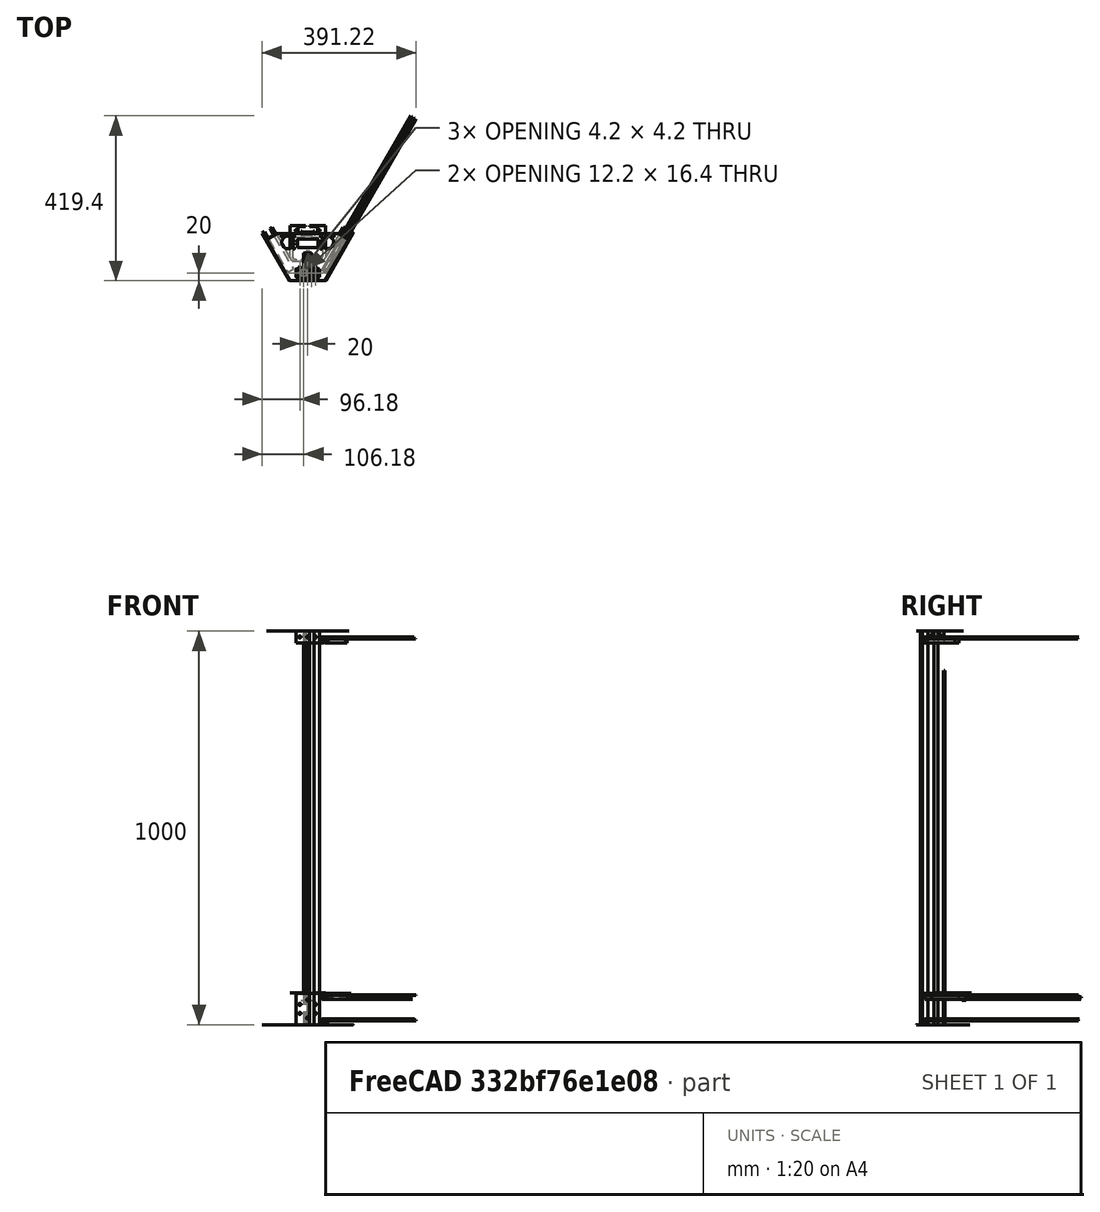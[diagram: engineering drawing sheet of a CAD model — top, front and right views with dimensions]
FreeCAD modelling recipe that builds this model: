
FCSTD DOCUMENT  (FreeCAD 2022.430R26244 +4758 (Git))
Label: SubAs3Column
License: All rights reserved
LicenseURL: http://en.wikipedia.org/wiki/All_rights_reserved
objects: App::FeaturePython×82, Part::FeaturePython×48, App::Link×8, App::LinkElement×3
note: 47 computed .brp shape members not serialized (recipe doc carries the construction recipe); baked Part::Feature solids carry a one-line shape summary decoded from their .brp
EXTERNAL_REF file=as3bottom_corner-M3x10.FCStd obj=Assembly
EXTERNAL_REF file=as3V-Slot 20x40x1000 Linear Rail.FCStd obj=Assembly
EXTERNAL_REF file=as3V-Slot 20x60x1000 Linear Rail.FCStd obj=Assembly
EXTERNAL_REF file=as3OpenBeam450mm.FCStd obj=Assembly
EXTERNAL_REF file=as3MotorFrame.FCStd obj=Assembly
EXTERNAL_REF file=As3NEMA 17.FCStd obj=Assembly
EXTERNAL_REF file=As3TopCorner.FCStd obj=Assembly
EXTERNAL_REF file=as3MGNR9R900CM-HiwinCorporation-3D-10-31-2021.FCStd obj=Assembly

FEATURE [App::Link] Link  label="As3bottom_corner-M3x10"
  AutoLinkLabel = false
  AutoPlacement = true
  LinkedObject = -> <external as3bottom_corner-M3x10.FCStd>#Assembly
  SyncGroupVisibility = false
  TreeRank = 0
  _LinkOwner = 170
  _LinkVersion = 1
FEATURE [App::Link] Link001  label="As3V-Slot 20x40x1000 Linear Rail"
  AutoLinkLabel = false
  AutoPlacement = true
  LinkPlacement = pos=(3.1367e-12,50,0) rot=(0,0,1;0rad)
  LinkedObject = -> <external as3V-Slot 20x40x1000 Linear Rail.FCStd>#Assembly
  Placement = pos=(3.1367e-12,50,0) rot=(0,0,1;0rad)
  SyncGroupVisibility = false
  TreeRank = 0
  _LinkOwner = 170
  _LinkVersion = 1
FEATURE [App::Link] Link002  label="As3V-Slot 20x60x1000 Linear Rail"
  AutoLinkLabel = false
  AutoPlacement = true
  LinkPlacement = pos=(0.1,20,1.28e-14) rot=(0,0,1;1.5708rad)
  LinkedObject = -> <external as3V-Slot 20x60x1000 Linear Rail.FCStd>#Assembly
  Placement = pos=(0.1,20,1.28e-14) rot=(0,0,1;1.5708rad)
  SyncGroupVisibility = false
  TreeRank = 0
  _LinkOwner = 170
  _LinkVersion = 1
FEATURE [App::LinkElement] Link003_i0
  LinkPlacement = pos=(310.961,131.486,64) rot=(0.866025,0.5,0;3.14159rad)
  LinkedObject = -> <external as3OpenBeam450mm.FCStd>#Assembly
  Placement = pos=(310.961,131.486,64) rot=(0.866025,0.5,0;3.14159rad)
  TreeRank = 0
  _LinkOwner = 191
  _LinkVersion = 1
FEATURE [App::LinkElement] Link003_i1
  LinkPlacement = pos=(1.39218,310.216,16) rot=(0,0,1;1.0472rad)
  LinkedObject = -> <external as3OpenBeam450mm.FCStd>#Assembly
  Placement = pos=(1.39218,310.216,16) rot=(0,0,1;1.0472rad)
  TreeRank = 0
  _LinkOwner = 191
  _LinkVersion = 1
FEATURE [App::LinkElement] Link003_i2
  LinkPlacement = pos=(0.13852,308.365,986) rot=(0,0,1;1.0472rad)
  LinkedObject = -> <external as3OpenBeam450mm.FCStd>#Assembly
  Placement = pos=(0.13852,308.365,986) rot=(0,0,1;1.0472rad)
  TreeRank = 0
  _LinkOwner = 191
  _LinkVersion = 1
FEATURE [App::Link] Link003  label="As3OpenBeam450mm"
  AutoLinkLabel = false
  AutoPlacement = true
  ElementCount = 3
  ElementList = -> [Link003_i0,Link003_i1,Link003_i2]
  LinkedObject = -> <external as3OpenBeam450mm.FCStd>#Assembly
  SyncGroupVisibility = false
  TreeRank = 0
  _LinkOwner = 170
  _LinkVersion = 1
FEATURE [App::Link] Link004  label="As3motorFrame"
  AutoLinkLabel = false
  AutoPlacement = true
  LinkPlacement = pos=(1.81557e-11,50.2887,11) rot=(0,0,1;0rad)
  LinkedObject = -> <external as3MotorFrame.FCStd>#Assembly
  Placement = pos=(1.81557e-11,50.2887,11) rot=(0,0,1;0rad)
  SyncGroupVisibility = false
  TreeRank = 0
  _LinkOwner = 170
  _LinkVersion = 1
FEATURE [App::Link] Link005  label="As3NEMA 17"
  AutoLinkLabel = false
  AutoPlacement = true
  LinkPlacement = pos=(-10.3955,158.351,45.6172) rot=(0,-0.707107,0.707107;3.14159rad)
  LinkedObject = -> <external As3NEMA 17.FCStd>#Assembly
  Placement = pos=(-10.3955,158.351,45.6172) rot=(0,-0.707107,0.707107;3.14159rad)
  SyncGroupVisibility = false
  TreeRank = 0
  _LinkOwner = 170
  _LinkVersion = 1
FEATURE [App::Link] Link006  label="As3top_corner"
  AutoLinkLabel = false
  AutoPlacement = true
  LinkPlacement = pos=(4.59e-14,11,1000) rot=(0,-1,0;3.14159rad)
  LinkedObject = -> <external As3TopCorner.FCStd>#Assembly
  Placement = pos=(4.59e-14,11,1000) rot=(0,-1,0;3.14159rad)
  SyncGroupVisibility = false
  TreeRank = 0
  _LinkOwner = 170
  _LinkVersion = 1
FEATURE [App::Link] Link007  label="As3MGNR9R900CM-HiwinCorporation-3D-10-31-2021"
  AutoLinkLabel = false
  AutoPlacement = true
  LinkPlacement = pos=(3.296e-12,69.5,892.5) rot=(0.57735,-0.57735,-0.57735;4.18879rad)
  LinkedObject = -> <external as3MGNR9R900CM-HiwinCorporation-3D-10-31-2021.FCStd>#Assembly
  Placement = pos=(3.296e-12,69.5,892.5) rot=(0.57735,-0.57735,-0.57735;4.18879rad)
  SyncGroupVisibility = false
  TreeRank = 0
  _LinkOwner = 170
  _LinkVersion = 1
FEATURE [Part::FeaturePython] Parts  # WARN: FeaturePython — macro-defined, semantics opaque (R4)
  Group = -> [Link,Link002,Link003,Link004,Link005,Link006,Link001,Link007]
  GroupMode = 0
  TreeRank = 0
  _LinkVersion = 1
FEATURE [Part::FeaturePython] Assembly  label="SubAs3Column"  # WARN: FeaturePython — macro-defined, semantics opaque (R4)
  AutoRelax = true
  BuildShape = 0
  Freeze = false
  Group = -> [Constraints,Elements,Parts]
  TreeRank = 0
  Verbose = false
  _LinkVersion = 1
  _SolverType = 1
  _Version = 1
FEATURE [App::FeaturePython] Constraints  # WARN: FeaturePython — macro-defined, semantics opaque (R4)
  Group = -> [Constraint,Constraint001,Constraint002,Constraint003,Constraint004,Constraint005,Constraint006,Constraint007,Constraint008,Constraint009,Constraint010,Constraint011,Constraint012,Constraint013,Constraint014,Constraint016,Constraint017,Constraint015,Constraint019,Constraint020,Constraint018,Constraint021,Constraint022,Constraint023,Constraint024,Constraint025,Constraint026]
  TreeRank = 0
  _LinkVersion = 1
  _Version = 1
FEATURE [App::FeaturePython] Elements  # WARN: FeaturePython — macro-defined, semantics opaque (R4)
  Group = -> [_Element,_Element001,_Element002,_Element003,_Element004,_Element005,_Element006,_Element007,_Element008,_Element009,_Element010,_Element011,_Element012,_Element013,_Element014,_Element015,_Element016,_Element017,_Element018,_Element019,_Element020,_Element021,_Element022,_Element023,_Element024,_Element025,_Element026,_Element027,_Element028,_Element029,_Element030,_Element031,_Element032,+13 more]
  TreeRank = 0
  _LinkVersion = 1
FEATURE [App::FeaturePython] Constraint  label="Locked"  # WARN: FeaturePython — macro-defined, semantics opaque (R4)
  Disabled = false
  Group = -> [ElementLink]
  TreeRank = 0
  _ConstraintType = 0
  _LinkVersion = 1
  _Parent = -> Constraints
FEATURE [App::FeaturePython] ElementLink  label="_Element"  # link proxy (typed FeaturePython)
  LinkTransform = true
  LinkedObject = -> _Element
  TreeRank = 0
  _LinkVersion = 1
  _Parent = -> Constraint
FEATURE [Part::FeaturePython] _Element  # link proxy (typed FeaturePython)
  Detach = false
  LinkTransform = true
  LinkedObject = -> Link [1.$FaceRef.]
  TreeRank = 0
  _LinkVersion = 1
  _Parent = -> Elements
FEATURE [App::FeaturePython] Constraint001  label="PlaneAlignment"  # WARN: FeaturePython — macro-defined, semantics opaque (R4)
  Angle = 0
  AnglePitch = 0
  AngleRoll = 0
  Cascade = false
  Disabled = false
  Group = -> [ElementLink001,ElementLink002]
  LockAngle = false
  TreeRank = 0
  _ConstraintType = 37
  _LinkVersion = 1
  _Parent = -> Constraints
FEATURE [App::FeaturePython] ElementLink001  label="_Element001"  # link proxy (typed FeaturePython)
  LinkTransform = true
  LinkedObject = -> _Element001
  TreeRank = 0
  _LinkVersion = 1
  _Parent = -> Constraint001
FEATURE [Part::FeaturePython] _Element001  # link proxy (typed FeaturePython)
  Detach = false
  LinkTransform = true
  LinkedObject = -> Link002 [1.$FaceVref.]
  TreeRank = 0
  _LinkVersion = 1
  _Parent = -> Elements
FEATURE [App::FeaturePython] ElementLink002  label="_Element002"  # link proxy (typed FeaturePython)
  LinkTransform = true
  LinkedObject = -> _Element002
  TreeRank = 0
  _LinkVersion = 1
  _Parent = -> Constraint001
FEATURE [Part::FeaturePython] _Element002  # link proxy (typed FeaturePython)
  Detach = false
  LinkTransform = true
  LinkedObject = -> Link [1.$AppuiPoteau1.]
  TreeRank = 0
  _LinkVersion = 1
  _Parent = -> Elements
FEATURE [App::FeaturePython] Constraint002  label="PlaneAlignment001"  # WARN: FeaturePython — macro-defined, semantics opaque (R4)
  Angle = 0
  AnglePitch = 0
  AngleRoll = 0
  Cascade = false
  Disabled = false
  Group = -> [ElementLink003,ElementLink004]
  LockAngle = false
  TreeRank = 0
  _ConstraintType = 37
  _LinkVersion = 1
  _Parent = -> Constraints
FEATURE [App::FeaturePython] ElementLink003  label="_Element003"  # link proxy (typed FeaturePython)
  LinkTransform = true
  LinkedObject = -> _Element003
  TreeRank = 0
  _LinkVersion = 1
  _Parent = -> Constraint002
FEATURE [Part::FeaturePython] _Element003  # link proxy (typed FeaturePython)
  Detach = false
  LinkTransform = true
  LinkedObject = -> Link002 [1.$FaceLat.]
  TreeRank = 0
  _LinkVersion = 1
  _Parent = -> Elements
FEATURE [App::FeaturePython] ElementLink004  label="_Element004"  # link proxy (typed FeaturePython)
  LinkTransform = true
  LinkedObject = -> _Element004
  TreeRank = 0
  _LinkVersion = 1
  _Parent = -> Constraint002
FEATURE [Part::FeaturePython] _Element004  # link proxy (typed FeaturePython)
  Detach = false
  LinkTransform = true
  LinkedObject = -> Link [1.$AppuiPoteau2.]
  TreeRank = 0
  _LinkVersion = 1
  _Parent = -> Elements
FEATURE [App::FeaturePython] Constraint003  label="PlaneAlignment002"  # WARN: FeaturePython — macro-defined, semantics opaque (R4)
  Angle = 0
  AnglePitch = 0
  AngleRoll = 0
  Cascade = false
  Disabled = false
  Group = -> [ElementLink005,ElementLink006]
  LockAngle = false
  TreeRank = 0
  _ConstraintType = 37
  _LinkVersion = 1
  _Parent = -> Constraints
FEATURE [App::FeaturePython] ElementLink005  label="_Element005"  # link proxy (typed FeaturePython)
  LinkTransform = true
  LinkedObject = -> _Element005
  TreeRank = 0
  _LinkVersion = 1
  _Parent = -> Constraint003
FEATURE [Part::FeaturePython] _Element005  # link proxy (typed FeaturePython)
  Detach = false
  LinkTransform = true
  LinkedObject = -> Link002 [1.$Extrem1.]
  TreeRank = 0
  _LinkVersion = 1
  _Parent = -> Elements
FEATURE [App::FeaturePython] ElementLink006  label="_Element"  # link proxy (typed FeaturePython)
  LinkTransform = true
  LinkedObject = -> _Element
  TreeRank = 0
  _LinkVersion = 1
  _Parent = -> Constraint003
FEATURE [App::FeaturePython] Constraint004  label="PlaneAlignment003"  # WARN: FeaturePython — macro-defined, semantics opaque (R4)
  Angle = 0
  AnglePitch = 0
  AngleRoll = 0
  Cascade = false
  Disabled = false
  Group = -> [ElementLink007,ElementLink008]
  LockAngle = false
  TreeRank = 0
  _ConstraintType = 37
  _LinkVersion = 1
  _Parent = -> Constraints
FEATURE [App::FeaturePython] ElementLink007  label="AppuiTrv1v@As3bottom_corner-M3x10@"  # link proxy (typed FeaturePython)
  LinkTransform = true
  LinkedObject = -> _Element006
  TreeRank = 0
  _LinkVersion = 1
  _Parent = -> Constraint004
FEATURE [Part::FeaturePython] _Element006  label="AppuiTrv1v@As3bottom_corner-M3x10@"  # link proxy (typed FeaturePython)
  Detach = false
  LinkTransform = true
  LinkedObject = -> Link [1.$AppuiTrav1v.]
  TreeRank = 0
  _LinkVersion = 1
  _Parent = -> Elements
FEATURE [App::FeaturePython] ElementLink008  label="FaceLat2@As3OpenBeam450mm@#0"  # link proxy (typed FeaturePython)
  LinkTransform = true
  LinkedObject = -> _Element016
  Placement = pos=(-5.68e-14,0,0) rot=(0,0,1;0rad)
  TreeRank = 0
  _LinkVersion = 1
  _Parent = -> Constraint004
FEATURE [Part::FeaturePython] _Element007  label="FaceLat@As3OpenBeam450mm@#0"  # link proxy (typed FeaturePython)
  Detach = false
  LinkTransform = true
  LinkedObject = -> Link003 [Link003_i0.1.$FaceLat1.]
  TreeRank = 0
  _LinkVersion = 1
  _Parent = -> Elements
FEATURE [App::FeaturePython] Constraint005  label="PlaneAlignment004"  # WARN: FeaturePython — macro-defined, semantics opaque (R4)
  Angle = 0
  AnglePitch = 0
  AngleRoll = 0
  Cascade = false
  Disabled = false
  Group = -> [ElementLink009,ElementLink010]
  LockAngle = false
  TreeRank = 0
  _ConstraintType = 37
  _LinkVersion = 1
  _Parent = -> Constraints
FEATURE [App::FeaturePython] ElementLink009  label="FaceHoriz@As3OpenBeam450mm@#0"  # link proxy (typed FeaturePython)
  LinkTransform = true
  LinkedObject = -> _Element008
  Placement = pos=(2.84e-14,-2.84e-14,0) rot=(0,0,1;0rad)
  TreeRank = 0
  _LinkVersion = 1
  _Parent = -> Constraint005
FEATURE [Part::FeaturePython] _Element008  label="FaceHoriz@As3OpenBeam450mm@#0"  # link proxy (typed FeaturePython)
  Detach = false
  LinkTransform = true
  LinkedObject = -> Link003 [Link003_i0.1.$FaceHoriz1.]
  TreeRank = 0
  _LinkVersion = 1
  _Parent = -> Elements
FEATURE [App::FeaturePython] ElementLink010  label="AppuiTrav1h@As3bottom_corner-M3x10@"  # link proxy (typed FeaturePython)
  LinkTransform = true
  LinkedObject = -> _Element009
  TreeRank = 0
  _LinkVersion = 1
  _Parent = -> Constraint005
FEATURE [Part::FeaturePython] _Element009  label="AppuiTrav1h@As3bottom_corner-M3x10@"  # link proxy (typed FeaturePython)
  Detach = false
  LinkTransform = true
  LinkedObject = -> Link [1.$AppuiTrav1h.]
  TreeRank = 0
  _LinkVersion = 1
  _Parent = -> Elements
FEATURE [App::FeaturePython] Constraint006  label="PlaneAlignment005"  # WARN: FeaturePython — macro-defined, semantics opaque (R4)
  Angle = 0
  AnglePitch = 0
  AngleRoll = 0
  Cascade = false
  Disabled = false
  Group = -> [ElementLink011,ElementLink012]
  LockAngle = false
  TreeRank = 0
  _ConstraintType = 37
  _LinkVersion = 1
  _Parent = -> Constraints
FEATURE [App::FeaturePython] ElementLink011  label="FaceHoriz@As3OpenBeam450mm@#1"  # link proxy (typed FeaturePython)
  LinkTransform = true
  LinkedObject = -> _Element010
  TreeRank = 0
  _LinkVersion = 1
  _Parent = -> Constraint006
FEATURE [Part::FeaturePython] _Element010  label="FaceHoriz@As3OpenBeam450mm@#1"  # link proxy (typed FeaturePython)
  Detach = false
  LinkTransform = true
  LinkedObject = -> Link003 [Link003_i1.1.$FaceHoriz1.]
  TreeRank = 0
  _LinkVersion = 1
  _Parent = -> Elements
FEATURE [App::FeaturePython] ElementLink012  label="AppuiTrav2h@As3bottom_corner-M3x10@"  # link proxy (typed FeaturePython)
  LinkTransform = true
  LinkedObject = -> _Element011
  TreeRank = 0
  _LinkVersion = 1
  _Parent = -> Constraint006
FEATURE [Part::FeaturePython] _Element011  label="AppuiTrav2h@As3bottom_corner-M3x10@"  # link proxy (typed FeaturePython)
  Detach = false
  LinkTransform = true
  LinkedObject = -> Link [1.$AppuiTrav2h.]
  TreeRank = 0
  _LinkVersion = 1
  _Parent = -> Elements
FEATURE [App::FeaturePython] Constraint007  label="PlaneAlignment006"  # WARN: FeaturePython — macro-defined, semantics opaque (R4)
  Angle = 0
  AnglePitch = 0
  AngleRoll = 0
  Cascade = false
  Disabled = false
  Group = -> [ElementLink013,ElementLink014]
  LockAngle = false
  TreeRank = 0
  _ConstraintType = 37
  _LinkVersion = 1
  _Parent = -> Constraints
FEATURE [App::FeaturePython] ElementLink013  label="AppuiTrv1v@As3bottom_corner-M3x10@"  # link proxy (typed FeaturePython)
  LinkTransform = true
  LinkedObject = -> _Element006
  Placement = pos=(0,1.42e-14,2.84e-14) rot=(0,0,1;0rad)
  TreeRank = 0
  _LinkVersion = 1
  _Parent = -> Constraint007
FEATURE [App::FeaturePython] ElementLink014  label="FaceLat@As3OpenBeam450mm@#1"  # link proxy (typed FeaturePython)
  LinkTransform = true
  LinkedObject = -> _Element012
  Placement = pos=(5.68e-14,-2.84e-14,-1.8e-15) rot=(0,0,1;0rad)
  TreeRank = 0
  _LinkVersion = 1
  _Parent = -> Constraint007
FEATURE [Part::FeaturePython] _Element012  label="FaceLat@As3OpenBeam450mm@#1"  # link proxy (typed FeaturePython)
  Detach = false
  LinkTransform = true
  LinkedObject = -> Link003 [Link003_i1.1.$FaceLat1.]
  TreeRank = 0
  _LinkVersion = 1
  _Parent = -> Elements
FEATURE [Part::FeaturePython] _Element013  label="Extrem1@As3OpenBeam450mm@#0"  # link proxy (typed FeaturePython)
  Detach = false
  LinkTransform = true
  LinkedObject = -> Link003 [Link003_i0.1.$Extrem1.]
  TreeRank = 0
  _LinkVersion = 1
  _Parent = -> Elements
FEATURE [Part::FeaturePython] _Element014  label="Extrem1@As3OpenBeam450mm@#1"  # link proxy (typed FeaturePython)
  Detach = false
  LinkTransform = true
  LinkedObject = -> Link003 [Link003_i1.1.$Extrem1.]
  TreeRank = 0
  _LinkVersion = 1
  _Parent = -> Elements
FEATURE [Part::FeaturePython] _Element015  label="ExtremRain1@As3bottom_corner-M3x10@"  # link proxy (typed FeaturePython)
  Detach = false
  LinkTransform = true
  LinkedObject = -> Link [1.$ExtremRain1.]
  TreeRank = 0
  _LinkVersion = 1
  _Parent = -> Elements
FEATURE [App::FeaturePython] Constraint008  label="PlaneAlignment007"  # WARN: FeaturePython — macro-defined, semantics opaque (R4)
  Angle = 0
  AnglePitch = 0
  AngleRoll = 0
  Cascade = false
  Disabled = false
  Group = -> [ElementLink015,ElementLink016]
  LockAngle = false
  TreeRank = 0
  _ConstraintType = 37
  _LinkVersion = 1
  _Parent = -> Constraints
FEATURE [App::FeaturePython] ElementLink015  label="ExtremRain1@As3bottom_corner-M3x10@"  # link proxy (typed FeaturePython)
  LinkTransform = true
  LinkedObject = -> _Element015
  TreeRank = 0
  _LinkVersion = 1
  _Parent = -> Constraint008
FEATURE [App::FeaturePython] ElementLink016  label="Extrem1@As3OpenBeam450mm@#0"  # link proxy (typed FeaturePython)
  LinkTransform = true
  LinkedObject = -> _Element013
  TreeRank = 0
  _LinkVersion = 1
  _Parent = -> Constraint008
FEATURE [App::FeaturePython] Constraint009  label="PlaneAlignment008"  # WARN: FeaturePython — macro-defined, semantics opaque (R4)
  Angle = 0
  AnglePitch = 0
  AngleRoll = 0
  Cascade = false
  Disabled = false
  Group = -> [ElementLink017,ElementLink018]
  LockAngle = false
  TreeRank = 0
  _ConstraintType = 37
  _LinkVersion = 1
  _Parent = -> Constraints
FEATURE [App::FeaturePython] ElementLink017  label="ExtremRain1@As3bottom_corner-M3x10@"  # link proxy (typed FeaturePython)
  LinkTransform = true
  LinkedObject = -> _Element015
  TreeRank = 0
  _LinkVersion = 1
  _Parent = -> Constraint009
FEATURE [App::FeaturePython] ElementLink018  label="Extrem1@As3OpenBeam450mm@#1"  # link proxy (typed FeaturePython)
  LinkTransform = true
  LinkedObject = -> _Element014
  TreeRank = 0
  _LinkVersion = 1
  _Parent = -> Constraint009
FEATURE [Part::FeaturePython] _Element016  label="FaceLat2@As3OpenBeam450mm@#0"  # link proxy (typed FeaturePython)
  Detach = false
  LinkTransform = true
  LinkedObject = -> Link003 [Link003_i0.1.$FaceLat2.]
  TreeRank = 0
  _LinkVersion = 1
  _Parent = -> Elements
FEATURE [App::FeaturePython] Constraint010  label="AxialAlignment"  # WARN: FeaturePython — macro-defined, semantics opaque (R4)
  Angle = 0
  AnglePitch = 0
  AngleRoll = 0
  Disabled = false
  Group = -> [ElementLink019,ElementLink020]
  LockAngle = false
  Multiply = false
  TreeRank = 0
  _ConstraintType = 36
  _LinkVersion = 1
  _Parent = -> Constraints
FEATURE [App::FeaturePython] ElementLink019  label="Fix1@As3motorFrame@"  # link proxy (typed FeaturePython)
  LinkTransform = true
  LinkedObject = -> _Element017
  TreeRank = 0
  _LinkVersion = 1
  _Parent = -> Constraint010
FEATURE [Part::FeaturePython] _Element017  label="Fix1@As3motorFrame@"  # link proxy (typed FeaturePython)
  Detach = false
  LinkTransform = true
  LinkedObject = -> Link004 [1.$Fix1.]
  TreeRank = 0
  _LinkVersion = 1
  _Parent = -> Elements
FEATURE [App::FeaturePython] ElementLink020  label="Fix@As3bottom_corner-M3x10@"  # link proxy (typed FeaturePython)
  LinkTransform = true
  LinkedObject = -> _Element018
  TreeRank = 0
  _LinkVersion = 1
  _Parent = -> Constraint010
FEATURE [Part::FeaturePython] _Element018  label="Fix@As3bottom_corner-M3x10@"  # link proxy (typed FeaturePython)
  Detach = false
  LinkTransform = true
  LinkedObject = -> Link [1.$FixM1.]
  TreeRank = 0
  _LinkVersion = 1
  _Parent = -> Elements
FEATURE [App::FeaturePython] Constraint011  label="SameOrientation"  # WARN: FeaturePython — macro-defined, semantics opaque (R4)
  Disabled = false
  Group = -> [ElementLink021,ElementLink022]
  TreeRank = 0
  _ConstraintType = 2
  _LinkVersion = 1
  _Parent = -> Constraints
FEATURE [App::FeaturePython] ElementLink021  label="_Element"  # link proxy (typed FeaturePython)
  LinkTransform = true
  LinkedObject = -> _Element
  TreeRank = 0
  _LinkVersion = 1
  _Parent = -> Constraint011
FEATURE [App::FeaturePython] ElementLink022  label="AppuiH1@As3motorFrame@"  # link proxy (typed FeaturePython)
  LinkTransform = true
  LinkedObject = -> _Element019
  Placement = pos=(-9.8e-15,-1.42e-14,0) rot=(0,0,1;0rad)
  TreeRank = 0
  _LinkVersion = 1
  _Parent = -> Constraint011
FEATURE [Part::FeaturePython] _Element019  label="AppuiH1@As3motorFrame@"  # link proxy (typed FeaturePython)
  Detach = false
  LinkTransform = true
  LinkedObject = -> Link004 [1.$AppuiH1.]
  TreeRank = 0
  _LinkVersion = 1
  _Parent = -> Elements
FEATURE [App::FeaturePython] Constraint012  label="AxialAlignment001"  # WARN: FeaturePython — macro-defined, semantics opaque (R4)
  Angle = 0
  AnglePitch = 0
  AngleRoll = 0
  Disabled = false
  Group = -> [ElementLink023,ElementLink024]
  LockAngle = false
  Multiply = false
  TreeRank = 0
  _ConstraintType = 36
  _LinkVersion = 1
  _Parent = -> Constraints
FEATURE [App::FeaturePython] ElementLink023  label="FixM2@As3bottom_corner-M3x10@"  # link proxy (typed FeaturePython)
  LinkTransform = true
  LinkedObject = -> _Element020
  TreeRank = 0
  _LinkVersion = 1
  _Parent = -> Constraint012
FEATURE [Part::FeaturePython] _Element020  label="FixM2@As3bottom_corner-M3x10@"  # link proxy (typed FeaturePython)
  Detach = false
  LinkTransform = true
  LinkedObject = -> Link [1.$FixM2.]
  TreeRank = 0
  _LinkVersion = 1
  _Parent = -> Elements
FEATURE [App::FeaturePython] ElementLink024  label="Fix2@As3motorFrame@"  # link proxy (typed FeaturePython)
  LinkTransform = true
  LinkedObject = -> _Element021
  TreeRank = 0
  _LinkVersion = 1
  _Parent = -> Constraint012
FEATURE [Part::FeaturePython] _Element021  label="Fix2@As3motorFrame@"  # link proxy (typed FeaturePython)
  Detach = false
  LinkTransform = true
  LinkedObject = -> Link004 [1.$Fix2.]
  TreeRank = 0
  _LinkVersion = 1
  _Parent = -> Elements
FEATURE [App::FeaturePython] Constraint013  label="PlaneCoincident"  # WARN: FeaturePython — macro-defined, semantics opaque (R4)
  Angle = 0
  AnglePitch = 0
  AngleRoll = 0
  Cascade = false
  Disabled = false
  Group = -> [ElementLink025,ElementLink026]
  LockAngle = false
  Multiply = false
  OffsetX = 0
  OffsetY = 0
  TreeRank = 0
  _ConstraintType = 35
  _LinkVersion = 1
  _Parent = -> Constraints
FEATURE [App::FeaturePython] ElementLink025  label="CentreMot@As3NEMA 17@"  # link proxy (typed FeaturePython)
  LinkTransform = true
  LinkedObject = -> _Element022
  TreeRank = 0
  _LinkVersion = 1
  _Parent = -> Constraint013
FEATURE [Part::FeaturePython] _Element022  label="CentreMot@As3NEMA 17@"  # link proxy (typed FeaturePython)
  Detach = false
  LinkTransform = true
  LinkedObject = -> Link005 [1.$CentreMot.]
  TreeRank = 0
  _LinkVersion = 1
  _Parent = -> Elements
FEATURE [App::FeaturePython] ElementLink026  label="CentrMot@As3motorFrame@"  # link proxy (typed FeaturePython)
  LinkTransform = true
  LinkedObject = -> _Element023
  TreeRank = 0
  _LinkVersion = 1
  _Parent = -> Constraint013
FEATURE [Part::FeaturePython] _Element023  label="CentrMot@As3motorFrame@"  # link proxy (typed FeaturePython)
  Detach = false
  LinkTransform = true
  LinkedObject = -> Link004 [1.$CentrMot.]
  TreeRank = 0
  _LinkVersion = 1
  _Parent = -> Elements
FEATURE [App::FeaturePython] Constraint014  label="SameOrientation001"  # WARN: FeaturePython — macro-defined, semantics opaque (R4)
  Disabled = false
  Group = -> [ElementLink027,ElementLink028]
  TreeRank = 0
  _ConstraintType = 2
  _LinkVersion = 1
  _Parent = -> Constraints
FEATURE [App::FeaturePython] ElementLink027  label="FaceH@As3NEMA 17@"  # link proxy (typed FeaturePython)
  LinkTransform = true
  LinkedObject = -> _Element024
  TreeRank = 0
  _LinkVersion = 1
  _Parent = -> Constraint014
FEATURE [Part::FeaturePython] _Element024  label="FaceH@As3NEMA 17@"  # link proxy (typed FeaturePython)
  Detach = false
  LinkTransform = true
  LinkedObject = -> Link005 [1.$FaceH.]
  TreeRank = 0
  _LinkVersion = 1
  _Parent = -> Elements
FEATURE [App::FeaturePython] ElementLink028  label="AppuiH1@As3motorFrame@"  # link proxy (typed FeaturePython)
  LinkTransform = true
  LinkedObject = -> _Element019
  TreeRank = 0
  _LinkVersion = 1
  _Parent = -> Constraint014
FEATURE [App::FeaturePython] Constraint015  label="PlaneAlignment009"  # WARN: FeaturePython — macro-defined, semantics opaque (R4)
  Angle = 0
  AnglePitch = 0
  AngleRoll = 0
  Cascade = false
  Disabled = false
  Group = -> [ElementLink029,ElementLink030]
  LockAngle = false
  TreeRank = 0
  _ConstraintType = 37
  _LinkVersion = 1
  _Parent = -> Constraints
FEATURE [App::FeaturePython] ElementLink029  label="Extrem2@As3V-Slot 20x60x1000 Linear Rail@"  # link proxy (typed FeaturePython)
  LinkTransform = true
  LinkedObject = -> _Element025
  TreeRank = 0
  _LinkVersion = 1
  _Parent = -> Constraint015
FEATURE [Part::FeaturePython] _Element025  label="Extrem2@As3V-Slot 20x60x1000 Linear Rail@"  # link proxy (typed FeaturePython)
  Detach = false
  LinkTransform = true
  LinkedObject = -> Link002 [1.$Extrem2.]
  TreeRank = 0
  _LinkVersion = 1
  _Parent = -> Elements
FEATURE [App::FeaturePython] ElementLink030  label="FaceHsup@As3top_corner@"  # link proxy (typed FeaturePython)
  LinkTransform = true
  LinkedObject = -> _Element026
  TreeRank = 0
  _LinkVersion = 1
  _Parent = -> Constraint015
FEATURE [Part::FeaturePython] _Element026  label="FaceHsup@As3top_corner@"  # link proxy (typed FeaturePython)
  Detach = false
  LinkTransform = true
  LinkedObject = -> Link006 [1.$FaceHsup.]
  TreeRank = 0
  _LinkVersion = 1
  _Parent = -> Elements
FEATURE [App::FeaturePython] Constraint016  label="PlaneAlignment010"  # WARN: FeaturePython — macro-defined, semantics opaque (R4)
  Angle = 0
  AnglePitch = 0
  AngleRoll = 0
  Cascade = false
  Disabled = false
  Group = -> [ElementLink031,ElementLink032]
  LockAngle = false
  TreeRank = 0
  _ConstraintType = 37
  _LinkVersion = 1
  _Parent = -> Constraints
FEATURE [App::FeaturePython] ElementLink031  label="_Element001"  # link proxy (typed FeaturePython)
  LinkTransform = true
  LinkedObject = -> _Element001
  TreeRank = 0
  _LinkVersion = 1
  _Parent = -> Constraint016
FEATURE [App::FeaturePython] ElementLink032  label="AppuiPoteau1@As3top_corner@"  # link proxy (typed FeaturePython)
  LinkTransform = true
  LinkedObject = -> _Element027
  TreeRank = 0
  _LinkVersion = 1
  _Parent = -> Constraint016
FEATURE [Part::FeaturePython] _Element027  label="AppuiPoteau1@As3top_corner@"  # link proxy (typed FeaturePython)
  Detach = false
  LinkTransform = true
  LinkedObject = -> Link006 [1.$AppuiPoteau1.]
  TreeRank = 0
  _LinkVersion = 1
  _Parent = -> Elements
FEATURE [App::FeaturePython] Constraint017  label="PlaneAlignment011"  # WARN: FeaturePython — macro-defined, semantics opaque (R4)
  Angle = 0
  AnglePitch = 0
  AngleRoll = 0
  Cascade = false
  Disabled = false
  Group = -> [ElementLink033,ElementLink034]
  LockAngle = false
  TreeRank = 0
  _ConstraintType = 37
  _LinkVersion = 1
  _Parent = -> Constraints
FEATURE [App::FeaturePython] ElementLink033  label="AppuiPoteau2@As3top_corner@"  # link proxy (typed FeaturePython)
  LinkTransform = true
  LinkedObject = -> _Element028
  TreeRank = 0
  _LinkVersion = 1
  _Parent = -> Constraint017
FEATURE [Part::FeaturePython] _Element028  label="AppuiPoteau2@As3top_corner@"  # link proxy (typed FeaturePython)
  Detach = false
  LinkTransform = true
  LinkedObject = -> Link006 [1.$AppuiPoteau2.]
  TreeRank = 0
  _LinkVersion = 1
  _Parent = -> Elements
FEATURE [App::FeaturePython] ElementLink034  label="_Element003"  # link proxy (typed FeaturePython)
  LinkTransform = true
  LinkedObject = -> _Element003
  TreeRank = 0
  _LinkVersion = 1
  _Parent = -> Constraint017
FEATURE [App::FeaturePython] Constraint018  label="PlaneAlignment014"  # WARN: FeaturePython — macro-defined, semantics opaque (R4)
  Angle = 0
  AnglePitch = 0
  AngleRoll = 0
  Cascade = false
  Disabled = false
  Group = -> [ElementLink035,ElementLink036]
  LockAngle = false
  TreeRank = 0
  _ConstraintType = 37
  _LinkVersion = 1
  _Parent = -> Constraints
FEATURE [App::FeaturePython] ElementLink035  label="Extrem1@As3OpenBeam450mm@#2"  # link proxy (typed FeaturePython)
  LinkTransform = true
  LinkedObject = -> _Element029
  TreeRank = 0
  _LinkVersion = 1
  _Parent = -> Constraint018
FEATURE [Part::FeaturePython] _Element029  label="Extrem1@As3OpenBeam450mm@#2"  # link proxy (typed FeaturePython)
  Detach = false
  LinkTransform = true
  LinkedObject = -> Link003 [Link003_i2.1.$Extrem1.]
  TreeRank = 0
  _LinkVersion = 1
  _Parent = -> Elements
FEATURE [App::FeaturePython] ElementLink036  label="AppuiTravExtr1@As3top_corner@"  # link proxy (typed FeaturePython)
  LinkTransform = true
  LinkedObject = -> _Element030
  TreeRank = 0
  _LinkVersion = 1
  _Parent = -> Constraint018
FEATURE [Part::FeaturePython] _Element030  label="AppuiTravExtr1@As3top_corner@"  # link proxy (typed FeaturePython)
  Detach = false
  LinkTransform = true
  LinkedObject = -> Link006 [1.$AppuiTravExtr1.]
  TreeRank = 0
  _LinkVersion = 1
  _Parent = -> Elements
FEATURE [App::FeaturePython] Constraint019  label="PlaneAlignment012"  # WARN: FeaturePython — macro-defined, semantics opaque (R4)
  Angle = 0
  AnglePitch = 0
  AngleRoll = 0
  Cascade = false
  Disabled = false
  Group = -> [ElementLink037,ElementLink038]
  LockAngle = false
  TreeRank = 0
  _ConstraintType = 37
  _LinkVersion = 1
  _Parent = -> Constraints
FEATURE [App::FeaturePython] ElementLink037  label="FaceLat1@As3OpenBeam450mm@#2"  # link proxy (typed FeaturePython)
  LinkTransform = true
  LinkedObject = -> _Element031
  TreeRank = 0
  _LinkVersion = 1
  _Parent = -> Constraint019
FEATURE [Part::FeaturePython] _Element031  label="FaceLat1@As3OpenBeam450mm@#2"  # link proxy (typed FeaturePython)
  Detach = false
  LinkTransform = true
  LinkedObject = -> Link003 [Link003_i2.1.$FaceLat1.]
  TreeRank = 0
  _LinkVersion = 1
  _Parent = -> Elements
FEATURE [App::FeaturePython] ElementLink038  label="AppuiTrav2v@As3top_corner@"  # link proxy (typed FeaturePython)
  LinkTransform = true
  LinkedObject = -> _Element032
  TreeRank = 0
  _LinkVersion = 1
  _Parent = -> Constraint019
FEATURE [Part::FeaturePython] _Element032  label="AppuiTrav2v@As3top_corner@"  # link proxy (typed FeaturePython)
  Detach = false
  LinkTransform = true
  LinkedObject = -> Link006 [1.$AppuiTrav2v.]
  TreeRank = 0
  _LinkVersion = 1
  _Parent = -> Elements
FEATURE [App::FeaturePython] Constraint020  label="PlaneAlignment013"  # WARN: FeaturePython — macro-defined, semantics opaque (R4)
  Angle = 0
  AnglePitch = 0
  AngleRoll = 0
  Cascade = false
  Disabled = false
  Group = -> [ElementLink039,ElementLink040]
  LockAngle = false
  TreeRank = 0
  _ConstraintType = 37
  _LinkVersion = 1
  _Parent = -> Constraints
FEATURE [App::FeaturePython] ElementLink039  label="AppuiTrav1h@As3top_corner@"  # link proxy (typed FeaturePython)
  LinkTransform = true
  LinkedObject = -> _Element033
  TreeRank = 0
  _LinkVersion = 1
  _Parent = -> Constraint020
FEATURE [Part::FeaturePython] _Element033  label="AppuiTrav1h@As3top_corner@"  # link proxy (typed FeaturePython)
  Detach = false
  LinkTransform = true
  LinkedObject = -> Link006 [1.$AppuiTrav1h.]
  TreeRank = 0
  _LinkVersion = 1
  _Parent = -> Elements
FEATURE [App::FeaturePython] ElementLink040  label="FaceHoriz1@As3OpenBeam450mm@#2"  # link proxy (typed FeaturePython)
  LinkTransform = true
  LinkedObject = -> _Element034
  TreeRank = 0
  _LinkVersion = 1
  _Parent = -> Constraint020
FEATURE [Part::FeaturePython] _Element034  label="FaceHoriz1@As3OpenBeam450mm@#2"  # link proxy (typed FeaturePython)
  Detach = false
  LinkTransform = true
  LinkedObject = -> Link003 [Link003_i2.1.$FaceHoriz1.]
  TreeRank = 0
  _LinkVersion = 1
  _Parent = -> Elements
FEATURE [App::FeaturePython] Constraint021  label="PlaneAlignment015"  # WARN: FeaturePython — macro-defined, semantics opaque (R4)
  Angle = 0
  AnglePitch = 0
  AngleRoll = 0
  Cascade = false
  Disabled = false
  Group = -> [ElementLink041,ElementLink042]
  LockAngle = false
  TreeRank = 0
  _ConstraintType = 37
  _LinkVersion = 1
  _Parent = -> Constraints
FEATURE [App::FeaturePython] ElementLink041  label="_Element"  # link proxy (typed FeaturePython)
  LinkTransform = true
  LinkedObject = -> _Element
  TreeRank = 0
  _LinkVersion = 1
  _Parent = -> Constraint021
FEATURE [App::FeaturePython] ElementLink042  label="Etrem1@As3V-Slot 20x40x1000 Linear Rail@"  # link proxy (typed FeaturePython)
  LinkTransform = true
  LinkedObject = -> _Element035
  TreeRank = 0
  _LinkVersion = 1
  _Parent = -> Constraint021
FEATURE [Part::FeaturePython] _Element035  label="Etrem1@As3V-Slot 20x40x1000 Linear Rail@"  # link proxy (typed FeaturePython)
  Detach = false
  LinkTransform = true
  LinkedObject = -> Link001 [1.$Etrem1.]
  TreeRank = 0
  _LinkVersion = 1
  _Parent = -> Elements
FEATURE [App::FeaturePython] Constraint022  label="PlaneAlignment016"  # WARN: FeaturePython — macro-defined, semantics opaque (R4)
  Angle = 0
  AnglePitch = 0
  AngleRoll = 0
  Cascade = false
  Disabled = false
  Group = -> [ElementLink043,ElementLink044]
  LockAngle = false
  TreeRank = 0
  _ConstraintType = 37
  _LinkVersion = 1
  _Parent = -> Constraints
FEATURE [App::FeaturePython] ElementLink043  label="FaceVref2@As3V-Slot 20x60x1000 Linear Rail@"  # link proxy (typed FeaturePython)
  LinkTransform = true
  LinkedObject = -> _Element036
  TreeRank = 0
  _LinkVersion = 1
  _Parent = -> Constraint022
FEATURE [Part::FeaturePython] _Element036  label="FaceVref2@As3V-Slot 20x60x1000 Linear Rail@"  # link proxy (typed FeaturePython)
  Detach = false
  LinkTransform = true
  LinkedObject = -> Link002 [1.$FaceVref2.]
  TreeRank = 0
  _LinkVersion = 1
  _Parent = -> Elements
FEATURE [App::FeaturePython] ElementLink044  label="Lat1@As3V-Slot 20x40x1000 Linear Rail@"  # link proxy (typed FeaturePython)
  LinkTransform = true
  LinkedObject = -> _Element037
  TreeRank = 0
  _LinkVersion = 1
  _Parent = -> Constraint022
FEATURE [Part::FeaturePython] _Element037  label="Lat1@As3V-Slot 20x40x1000 Linear Rail@"  # link proxy (typed FeaturePython)
  Detach = false
  LinkTransform = true
  LinkedObject = -> Link001 [1.$Lat1.]
  TreeRank = 0
  _LinkVersion = 1
  _Parent = -> Elements
FEATURE [App::FeaturePython] Constraint023  label="PlaneAlignment017"  # WARN: FeaturePython — macro-defined, semantics opaque (R4)
  Angle = 0
  AnglePitch = 0
  AngleRoll = 0
  Cascade = false
  Disabled = false
  Group = -> [ElementLink045,ElementLink046]
  LockAngle = false
  TreeRank = 0
  _ConstraintType = 37
  _LinkVersion = 1
  _Parent = -> Constraints
FEATURE [App::FeaturePython] ElementLink045  label="FaceRef@As3V-Slot 20x40x1000 Linear Rail@"  # link proxy (typed FeaturePython)
  LinkTransform = true
  LinkedObject = -> _Element038
  TreeRank = 0
  _LinkVersion = 1
  _Parent = -> Constraint023
FEATURE [Part::FeaturePython] _Element038  label="FaceRef@As3V-Slot 20x40x1000 Linear Rail@"  # link proxy (typed FeaturePython)
  Detach = false
  LinkTransform = true
  LinkedObject = -> Link001 [1.$FaceRef.]
  TreeRank = 0
  _LinkVersion = 1
  _Parent = -> Elements
FEATURE [App::FeaturePython] ElementLink046  label="AppuiLatPoteau22@As3top_corner@"  # link proxy (typed FeaturePython)
  LinkTransform = true
  LinkedObject = -> _Element039
  TreeRank = 0
  _LinkVersion = 1
  _Parent = -> Constraint023
FEATURE [Part::FeaturePython] _Element039  label="AppuiLatPoteau22@As3top_corner@"  # link proxy (typed FeaturePython)
  Detach = false
  LinkTransform = true
  LinkedObject = -> Link006 [1.$AppuiLatPoteau22.]
  TreeRank = 0
  _LinkVersion = 1
  _Parent = -> Elements
FEATURE [App::FeaturePython] Constraint024  label="PlaneAlignment018"  # WARN: FeaturePython — macro-defined, semantics opaque (R4)
  Angle = 0
  AnglePitch = 0
  AngleRoll = 0
  Cascade = false
  Disabled = false
  Group = -> [ElementLink047,ElementLink048]
  LockAngle = false
  TreeRank = 0
  _ConstraintType = 37
  _LinkVersion = 1
  _Parent = -> Constraints
FEATURE [App::FeaturePython] ElementLink047  label="_Element"  # link proxy (typed FeaturePython)
  LinkTransform = true
  LinkedObject = -> _Element
  TreeRank = 0
  _LinkVersion = 1
  _Parent = -> Constraint024
FEATURE [App::FeaturePython] ElementLink048  label="Extrem1@As3MGNR9R900CM-HiwinCorporation-3D-10-31-2021@"  # link proxy (typed FeaturePython)
  LinkTransform = true
  LinkedObject = -> _Element040
  TreeRank = 0
  _LinkVersion = 1
  _Parent = -> Constraint024
FEATURE [Part::FeaturePython] _Element040  label="Extrem1@As3MGNR9R900CM-HiwinCorporation-3D-10-31-2021@"  # link proxy (typed FeaturePython)
  Detach = false
  LinkTransform = true
  LinkedObject = -> Link007 [1.$Extrem1.]
  TreeRank = 0
  _LinkVersion = 1
  _Parent = -> Elements
FEATURE [App::FeaturePython] Constraint025  label="PlaneAlignment019"  # WARN: FeaturePython — macro-defined, semantics opaque (R4)
  Angle = 0
  AnglePitch = 0
  AngleRoll = 0
  Cascade = false
  Disabled = false
  Group = -> [ElementLink049,ElementLink050]
  LockAngle = false
  Offset = 39.5
  TreeRank = 0
  _ConstraintType = 37
  _LinkVersion = 1
  _Parent = -> Constraints
FEATURE [App::FeaturePython] ElementLink049  label="Ref@As3MGNR9R900CM-HiwinCorporation-3D-10-31-2021@"  # link proxy (typed FeaturePython)
  LinkTransform = true
  LinkedObject = -> _Element041
  TreeRank = 0
  _LinkVersion = 1
  _Parent = -> Constraint025
FEATURE [Part::FeaturePython] _Element041  label="Ref@As3MGNR9R900CM-HiwinCorporation-3D-10-31-2021@"  # link proxy (typed FeaturePython)
  Detach = false
  LinkTransform = true
  LinkedObject = -> Link007 [1.$Ref.]
  TreeRank = 0
  _LinkVersion = 1
  _Parent = -> Elements
FEATURE [App::FeaturePython] ElementLink050  label="Lat1@As3V-Slot 20x40x1000 Linear Rail@"  # link proxy (typed FeaturePython)
  LinkTransform = true
  LinkedObject = -> _Element037
  TreeRank = 0
  _LinkVersion = 1
  _Parent = -> Constraint025
FEATURE [App::FeaturePython] Constraint026  label="PlaneAlignment020"  # WARN: FeaturePython — macro-defined, semantics opaque (R4)
  Angle = 0
  AnglePitch = 0
  AngleRoll = 0
  Cascade = false
  Disabled = false
  Group = -> [ElementLink051,ElementLink052]
  LockAngle = false
  Offset = 5.5
  TreeRank = 0
  _ConstraintType = 37
  _LinkVersion = 1
  _Parent = -> Constraints
FEATURE [App::FeaturePython] ElementLink051  label="Lat@As3MGNR9R900CM-HiwinCorporation-3D-10-31-2021@"  # link proxy (typed FeaturePython)
  LinkTransform = true
  LinkedObject = -> _Element042
  TreeRank = 0
  _LinkVersion = 1
  _Parent = -> Constraint026
FEATURE [Part::FeaturePython] _Element042  label="Lat@As3MGNR9R900CM-HiwinCorporation-3D-10-31-2021@"  # link proxy (typed FeaturePython)
  Detach = false
  LinkTransform = true
  LinkedObject = -> Link007 [1.$Lat.]
  TreeRank = 0
  _LinkVersion = 1
  _Parent = -> Elements
FEATURE [App::FeaturePython] ElementLink052  label="FaceRef@As3V-Slot 20x40x1000 Linear Rail@"  # link proxy (typed FeaturePython)
  LinkTransform = true
  LinkedObject = -> _Element038
  TreeRank = 0
  _LinkVersion = 1
  _Parent = -> Constraint026
FEATURE [Part::FeaturePython] Element  label="Fix3@As3motorFrame@"  # link proxy (typed FeaturePython)
  Detach = false
  LinkTransform = true
  LinkedObject = -> Link004 [1.$Fix3.]
  TreeRank = 0
  _LinkVersion = 1
  _Parent = -> Elements
FEATURE [Part::FeaturePython] Element001  label="Fix4@As3motorFrame@"  # link proxy (typed FeaturePython)
  Detach = false
  LinkTransform = true
  LinkedObject = -> Link004 [1.$Fix4.]
  TreeRank = 0
  _LinkVersion = 1
  _Parent = -> Elements
FEATURE [Part::FeaturePython] Element002  label="Fix@As3MGNR9R900CM-HiwinCorporation-3D-10-31-2021@"  # link proxy (typed FeaturePython)
  Detach = false
  LinkTransform = true
  LinkedObject = -> Link007 [1.$Fix.]
  TreeRank = 0
  _LinkVersion = 1
  _Parent = -> Elements

RESOLVED EXTERNAL PARTS (link-assembly join: the EXTERNAL_REF files above that resolve inside this repo's crawl, each included once):
---- part As3TopCorner.FCStd = doc fcstd_daefd770ef8e ----
FCSTD DOCUMENT  (FreeCAD 2022.430R26244 +4758 (Git))
Label: As3TopCorner
License: All rights reserved
LicenseURL: http://en.wikipedia.org/wiki/All_rights_reserved
objects: Part::FeaturePython×12, App::FeaturePython×2, Part::Feature×1
note: 12 computed .brp shape members not serialized (recipe doc carries the construction recipe); baked Part::Feature solids carry a one-line shape summary decoded from their .brp

FEATURE [App::FeaturePython] Constraints  # WARN: FeaturePython — macro-defined, semantics opaque (R4)
  TreeRank = 0
  _LinkVersion = 1
  _Version = 1
FEATURE [Part::Feature] ShapeCopy  label="TopCorner"
  Placement = pos=(-1.75e-14,-0.999998,-2.49e-14) rot=(0,0,1;0rad)
  TreeRank = 6
  shape: bbox 211.8 x 120.4 x 30 mm, 156 faces (baked)
FEATURE [Part::FeaturePython] Parts  # WARN: FeaturePython — macro-defined, semantics opaque (R4)
  Group = -> [ShapeCopy]
  GroupMode = 0
  TreeRank = 0
  _LinkVersion = 1
FEATURE [Part::FeaturePython] Assembly  label="As3TopCorner"  # WARN: FeaturePython — macro-defined, semantics opaque (R4)
  AutoRelax = true
  BuildShape = 0
  Freeze = false
  Group = -> [Constraints,Elements,Parts]
  TreeRank = 0
  Verbose = false
  _LinkVersion = 1
  _SolverType = 1
  _Version = 1
FEATURE [App::FeaturePython] Elements  # WARN: FeaturePython — macro-defined, semantics opaque (R4)
  Group = -> [Element,Element001,Element002,Element004,Element005,Element006,Element007,Element008,Element009,Element010]
  TreeRank = 0
  _LinkVersion = 1
FEATURE [Part::FeaturePython] Element  label="FaceHsup"  # link proxy (typed FeaturePython)
  Detach = false
  LinkTransform = true
  LinkedObject = -> ShapeCopy [Face23]
  TreeRank = 0
  _LinkVersion = 1
  _Parent = -> Elements
FEATURE [Part::FeaturePython] Element001  label="AppuiPoteau1"  # link proxy (typed FeaturePython)
  Detach = false
  LinkTransform = true
  LinkedObject = -> ShapeCopy [Face46]
  TreeRank = 0
  _LinkVersion = 1
  _Parent = -> Elements
FEATURE [Part::FeaturePython] Element002  label="AppuiPoteau2"  # link proxy (typed FeaturePython)
  Detach = false
  LinkTransform = true
  LinkedObject = -> ShapeCopy [Face44]
  TreeRank = 0
  _LinkVersion = 1
  _Parent = -> Elements
FEATURE [Part::FeaturePython] Element004  label="AppuiTravExtr1"  # link proxy (typed FeaturePython)
  Detach = false
  LinkTransform = true
  LinkedObject = -> ShapeCopy [Face18]
  TreeRank = 0
  _LinkVersion = 1
  _Parent = -> Elements
FEATURE [Part::FeaturePython] Element005  label="AppuiTrav1h"  # link proxy (typed FeaturePython)
  Detach = false
  LinkTransform = true
  LinkedObject = -> ShapeCopy [Face77]
  TreeRank = 0
  _LinkVersion = 1
  _Parent = -> Elements
FEATURE [Part::FeaturePython] Element006  label="AppuiTravExtr2"  # link proxy (typed FeaturePython)
  Detach = false
  LinkTransform = true
  LinkedObject = -> ShapeCopy [Face25]
  TreeRank = 0
  _LinkVersion = 1
  _Parent = -> Elements
FEATURE [Part::FeaturePython] Element007  label="AppuiTrav1v"  # link proxy (typed FeaturePython)
  Detach = false
  LinkTransform = true
  LinkedObject = -> ShapeCopy [Face27]
  TreeRank = 0
  _LinkVersion = 1
  _Parent = -> Elements
FEATURE [Part::FeaturePython] Element008  label="AppuiTrav2v"  # link proxy (typed FeaturePython)
  Detach = false
  LinkTransform = true
  LinkedObject = -> ShapeCopy [Face20]
  TreeRank = 0
  _LinkVersion = 1
  _Parent = -> Elements
FEATURE [Part::FeaturePython] Element009  label="AppuiLatPoteau21"  # link proxy (typed FeaturePython)
  Detach = false
  LinkTransform = true
  LinkedObject = -> ShapeCopy [Face33]
  TreeRank = 0
  _LinkVersion = 1
  _Parent = -> Elements
FEATURE [Part::FeaturePython] Element010  label="AppuiLatPoteau22"  # link proxy (typed FeaturePython)
  Detach = false
  LinkTransform = true
  LinkedObject = -> ShapeCopy [Face37]
  TreeRank = 0
  _LinkVersion = 1
  _Parent = -> Elements
---- part as3MGNR9R900CM-HiwinCorporation-3D-10-31-2021.FCStd = doc fcstd_1e4a78aefe62 ----
FCSTD DOCUMENT  (FreeCAD 2022.430R26244 +4758 (Git))
Label: as3MGNR9R900CM-HiwinCorporation-3D-10-31-2021
License: All rights reserved
LicenseURL: http://en.wikipedia.org/wiki/All_rights_reserved
objects: Part::FeaturePython×8, App::FeaturePython×2, Part::Feature×1
note: 8 computed .brp shape members not serialized (recipe doc carries the construction recipe); baked Part::Feature solids carry a one-line shape summary decoded from their .brp

FEATURE [Part::Feature] Solid  label="MGNR9R900CM-HiwinCorporation-3D-10-31-2021"
  TreeRank = 0
  shape: bbox 900 x 9 x 6.5 mm, 261 faces (baked)
FEATURE [App::FeaturePython] Constraints  # WARN: FeaturePython — macro-defined, semantics opaque (R4)
  TreeRank = 0
  _LinkVersion = 1
  _Version = 1
FEATURE [Part::FeaturePython] Parts  # WARN: FeaturePython — macro-defined, semantics opaque (R4)
  Group = -> [Solid]
  GroupMode = 0
  TreeRank = 0
  _LinkVersion = 1
FEATURE [Part::FeaturePython] Assembly  label="As3MGNR9R900CM-HiwinCorporation-3D-10-31-2021"  # WARN: FeaturePython — macro-defined, semantics opaque (R4)
  AutoRelax = true
  BuildShape = 0
  Freeze = false
  Group = -> [Constraints,Elements,Parts]
  TreeRank = 0
  Verbose = false
  _LinkVersion = 1
  _SolverType = 1
  _Version = 1
FEATURE [App::FeaturePython] Elements  # WARN: FeaturePython — macro-defined, semantics opaque (R4)
  Group = -> [Element,Element001,Element002,Element003,Element004,Element005]
  TreeRank = 0
  _LinkVersion = 1
FEATURE [Part::FeaturePython] Element  label="Extrem1"  # link proxy (typed FeaturePython)
  Detach = false
  LinkTransform = true
  LinkedObject = -> Solid [Face169]
  TreeRank = 0
  _LinkVersion = 1
  _Parent = -> Elements
FEATURE [Part::FeaturePython] Element001  label="Chanf1"  # link proxy (typed FeaturePython)
  Detach = false
  LinkTransform = true
  LinkedObject = -> Solid [Face89]
  TreeRank = 0
  _LinkVersion = 1
  _Parent = -> Elements
FEATURE [Part::FeaturePython] Element002  label="Chanf2"  # link proxy (typed FeaturePython)
  Detach = false
  LinkTransform = true
  LinkedObject = -> Solid [Face116]
  TreeRank = 0
  _LinkVersion = 1
  _Parent = -> Elements
FEATURE [Part::FeaturePython] Element003  label="Ref"  # link proxy (typed FeaturePython)
  Detach = false
  LinkTransform = true
  LinkedObject = -> Solid [Face119]
  TreeRank = 0
  _LinkVersion = 1
  _Parent = -> Elements
FEATURE [Part::FeaturePython] Element004  label="Lat"  # link proxy (typed FeaturePython)
  Detach = false
  LinkTransform = true
  LinkedObject = -> Solid [Face115]
  TreeRank = 0
  _LinkVersion = 1
  _Parent = -> Elements
FEATURE [Part::FeaturePython] Element005  label="Fix"  # link proxy (typed FeaturePython)
  Detach = false
  LinkTransform = true
  LinkedObject = -> Solid [Edge352]
  TreeRank = 0
  _LinkVersion = 1
  _Parent = -> Elements
---- part as3MotorFrame.FCStd = doc fcstd_3d83fece921b ----
FCSTD DOCUMENT  (FreeCAD 2022.430R26244 +4758 (Git))
Label: as3MotorFrame
License: All rights reserved
LicenseURL: http://en.wikipedia.org/wiki/All_rights_reserved
objects: Part::FeaturePython×8, App::FeaturePython×2, App::Link×1
note: 7 computed .brp shape members not serialized (recipe doc carries the construction recipe); baked Part::Feature solids carry a one-line shape summary decoded from their .brp
EXTERNAL_REF file=motor_frame.FCStd obj=ShapeCopy

FEATURE [App::FeaturePython] Constraints  # WARN: FeaturePython — macro-defined, semantics opaque (R4)
  TreeRank = 0
  _LinkVersion = 1
  _Version = 1
FEATURE [App::Link] Link  label="MotorFrame"
  AutoLinkLabel = false
  AutoPlacement = true
  LinkedObject = -> <external motor_frame.FCStd>#ShapeCopy
  SyncGroupVisibility = false
  TreeRank = 0
  _LinkOwner = 2961
  _LinkVersion = 1
FEATURE [Part::FeaturePython] Parts  # WARN: FeaturePython — macro-defined, semantics opaque (R4)
  Group = -> [Link]
  GroupMode = 0
  TreeRank = 0
  _LinkVersion = 1
FEATURE [Part::FeaturePython] Assembly  label="As3motorFrame"  # WARN: FeaturePython — macro-defined, semantics opaque (R4)
  AutoRelax = true
  BuildShape = 0
  Freeze = false
  Group = -> [Constraints,Elements,Parts]
  TreeRank = 0
  Verbose = false
  _LinkVersion = 1
  _SolverType = 1
  _Version = 1
FEATURE [App::FeaturePython] Elements  # WARN: FeaturePython — macro-defined, semantics opaque (R4)
  Group = -> [Element,Element001,Element002,Element003,Element004,Element005]
  TreeRank = 0
  _LinkVersion = 1
FEATURE [Part::FeaturePython] Element  label="Fix1"  # link proxy (typed FeaturePython)
  Detach = false
  LinkTransform = true
  LinkedObject = -> Link [Edge127]
  TreeRank = 0
  _LinkVersion = 1
  _Parent = -> Elements
FEATURE [Part::FeaturePython] Element001  label="Fix2"  # link proxy (typed FeaturePython)
  Detach = false
  LinkTransform = true
  LinkedObject = -> Link [Edge113]
  TreeRank = 0
  _LinkVersion = 1
  _Parent = -> Elements
FEATURE [Part::FeaturePython] Element002  label="AppuiH1"  # link proxy (typed FeaturePython)
  Detach = false
  LinkTransform = true
  LinkedObject = -> Link [Face5]
  TreeRank = 0
  _LinkVersion = 1
  _Parent = -> Elements
FEATURE [Part::FeaturePython] Element003  label="Fix3"  # link proxy (typed FeaturePython)
  Detach = false
  LinkTransform = true
  LinkedObject = -> Link [Edge53]
  TreeRank = 0
  _LinkVersion = 1
  _Parent = -> Elements
FEATURE [Part::FeaturePython] Element004  label="Fix4"  # link proxy (typed FeaturePython)
  Detach = false
  LinkTransform = true
  LinkedObject = -> Link [Edge54]
  TreeRank = 0
  _LinkVersion = 1
  _Parent = -> Elements
FEATURE [Part::FeaturePython] Element005  label="CentrMot"  # link proxy (typed FeaturePython)
  Detach = false
  LinkTransform = true
  LinkedObject = -> Link [Edge63]
  TreeRank = 0
  _LinkVersion = 1
  _Parent = -> Elements
---- part as3OpenBeam450mm.FCStd = doc fcstd_86945051230a ----
FCSTD DOCUMENT  (FreeCAD 2022.430R26244 +4758 (Git))
Label: as3OpenBeam450mm
License: All rights reserved
LicenseURL: http://en.wikipedia.org/wiki/All_rights_reserved
objects: Part::FeaturePython×9, App::FeaturePython×2
note: 8 computed .brp shape members not serialized (recipe doc carries the construction recipe); baked Part::Feature solids carry a one-line shape summary decoded from their .brp

FEATURE [Part::FeaturePython] b_OpenBeam450mm_001_  label="OpenBeam450mm"  # a2plus imported part (geometry in sourceFile) (typed FeaturePython)
  Placement = pos=(274.93,-178.73,-8.30001) rot=(0,-1,0;1.5708rad)
  TreeRank = 0
  a2p_Version = V0.1
  fixedPosition = false
  objectType = a2pPart
  sourceFile = .\OpenBeam450mm.FCStd
  subassemblyImport = false
  timeLastImport = 1.61981e+09
  updateColors = true
FEATURE [App::FeaturePython] Constraints  # WARN: FeaturePython — macro-defined, semantics opaque (R4)
  TreeRank = 0
  _LinkVersion = 1
  _Version = 1
FEATURE [Part::FeaturePython] Parts  # WARN: FeaturePython — macro-defined, semantics opaque (R4)
  Group = -> [b_OpenBeam450mm_001_]
  GroupMode = 0
  TreeRank = 0
  _LinkVersion = 1
FEATURE [Part::FeaturePython] Assembly  label="As3OpenBeam450mm"  # WARN: FeaturePython — macro-defined, semantics opaque (R4)
  AutoRelax = true
  BuildShape = 0
  Freeze = false
  Group = -> [Constraints,Elements,Parts]
  TreeRank = 0
  Verbose = false
  _LinkVersion = 1
  _SolverType = 1
  _Version = 1
FEATURE [App::FeaturePython] Elements  # WARN: FeaturePython — macro-defined, semantics opaque (R4)
  Group = -> [Element,Element001,Element002,Element003,Element004,Element005]
  TreeRank = 0
  _LinkVersion = 1
FEATURE [Part::FeaturePython] Element  label="Extrem1"  # link proxy (typed FeaturePython)
  Detach = false
  LinkTransform = true
  LinkedObject = -> b_OpenBeam450mm_001_ [Face16]
  TreeRank = 0
  _LinkVersion = 1
  _Parent = -> Elements
FEATURE [Part::FeaturePython] Element001  label="FaceHoriz1"  # link proxy (typed FeaturePython)
  Detach = false
  LinkTransform = true
  LinkedObject = -> b_OpenBeam450mm_001_ [Face18]
  TreeRank = 0
  _LinkVersion = 1
  _Parent = -> Elements
FEATURE [Part::FeaturePython] Element002  label="FaceLat1"  # link proxy (typed FeaturePython)
  Detach = false
  LinkTransform = true
  LinkedObject = -> b_OpenBeam450mm_001_ [Face5]
  TreeRank = 0
  _LinkVersion = 1
  _Parent = -> Elements
FEATURE [Part::FeaturePython] Element003  label="FaceHoriz2"  # link proxy (typed FeaturePython)
  Detach = false
  LinkTransform = true
  LinkedObject = -> b_OpenBeam450mm_001_ [Face20]
  TreeRank = 0
  _LinkVersion = 1
  _Parent = -> Elements
FEATURE [Part::FeaturePython] Element004  label="Extrem2"  # link proxy (typed FeaturePython)
  Detach = false
  LinkTransform = true
  LinkedObject = -> b_OpenBeam450mm_001_ [Face17]
  TreeRank = 0
  _LinkVersion = 1
  _Parent = -> Elements
FEATURE [Part::FeaturePython] Element005  label="FaceLat2"  # link proxy (typed FeaturePython)
  Detach = false
  LinkTransform = true
  LinkedObject = -> b_OpenBeam450mm_001_ [Face8]
  TreeRank = 0
  _LinkVersion = 1
  _Parent = -> Elements
---- part as3bottom_corner-M3x10.FCStd = doc fcstd_7aa3a1511274 ----
FCSTD DOCUMENT  (FreeCAD 2022.430R26244 +4758 (Git))
Label: as3bottom_corner-M3x10
License: All rights reserved
LicenseURL: http://en.wikipedia.org/wiki/All_rights_reserved
objects: Part::FeaturePython×13, App::FeaturePython×2, Part::Feature×1
note: 13 computed .brp shape members not serialized (recipe doc carries the construction recipe); baked Part::Feature solids carry a one-line shape summary decoded from their .brp

FEATURE [App::FeaturePython] Constraints  # WARN: FeaturePython — macro-defined, semantics opaque (R4)
  TreeRank = 0
  _LinkVersion = 1
  _Version = 1
FEATURE [Part::Feature] ShapeCopy  label="BottomCornerM3x10"
  TreeRank = 44
  shape: bbox 232.2 x 136.6 x 80 mm, 177 faces (baked)
FEATURE [Part::FeaturePython] Parts  # WARN: FeaturePython — macro-defined, semantics opaque (R4)
  Group = -> [ShapeCopy]
  GroupMode = 0
  TreeRank = 0
  _LinkVersion = 1
FEATURE [Part::FeaturePython] Assembly  label="As3BottomCorner-M3x10"  # WARN: FeaturePython — macro-defined, semantics opaque (R4)
  AutoRelax = true
  BuildShape = 0
  Freeze = false
  Group = -> [Constraints,Elements,Parts]
  TreeRank = 0
  Verbose = false
  _LinkVersion = 1
  _SolverType = 1
  _Version = 1
FEATURE [App::FeaturePython] Elements  # WARN: FeaturePython — macro-defined, semantics opaque (R4)
  Group = -> [Element,Element001,Element002,Element003,Element004,Element005,Element006,Element007,Element008,Element009,Element010]
  TreeRank = 0
  _LinkVersion = 1
FEATURE [Part::FeaturePython] Element  label="FaceRef"  # link proxy (typed FeaturePython)
  Detach = false
  LinkTransform = true
  LinkedObject = -> ShapeCopy [Face37]
  TreeRank = 0
  _LinkVersion = 1
  _Parent = -> Elements
FEATURE [Part::FeaturePython] Element001  label="AppuiPoteau1"  # link proxy (typed FeaturePython)
  Detach = false
  LinkTransform = true
  LinkedObject = -> ShapeCopy [Face9]
  TreeRank = 0
  _LinkVersion = 1
  _Parent = -> Elements
FEATURE [Part::FeaturePython] Element002  label="AppuiPoteau2"  # link proxy (typed FeaturePython)
  Detach = false
  LinkTransform = true
  LinkedObject = -> ShapeCopy [Face35]
  TreeRank = 0
  _LinkVersion = 1
  _Parent = -> Elements
FEATURE [Part::FeaturePython] Element003  label="AppuiTrav1v"  # link proxy (typed FeaturePython)
  Detach = false
  LinkTransform = true
  LinkedObject = -> ShapeCopy [Face51]
  TreeRank = 0
  _LinkVersion = 1
  _Parent = -> Elements
FEATURE [Part::FeaturePython] Element004  label="AppuiTrav1h"  # link proxy (typed FeaturePython)
  Detach = false
  LinkTransform = true
  LinkedObject = -> ShapeCopy [Face49]
  TreeRank = 0
  _LinkVersion = 1
  _Parent = -> Elements
FEATURE [Part::FeaturePython] Element005  label="AppuiTrav2h"  # link proxy (typed FeaturePython)
  Detach = false
  LinkTransform = true
  LinkedObject = -> ShapeCopy [Face45]
  TreeRank = 0
  _LinkVersion = 1
  _Parent = -> Elements
FEATURE [Part::FeaturePython] Element006  label="AppuiTrv2v"  # link proxy (typed FeaturePython)
  Detach = false
  LinkTransform = true
  LinkedObject = -> ShapeCopy [Face79]
  TreeRank = 0
  _LinkVersion = 1
  _Parent = -> Elements
FEATURE [Part::FeaturePython] Element007  label="ExtremRain1"  # link proxy (typed FeaturePython)
  Detach = false
  LinkTransform = true
  LinkedObject = -> ShapeCopy [Face12]
  TreeRank = 0
  _LinkVersion = 1
  _Parent = -> Elements
FEATURE [Part::FeaturePython] Element008  label="ExtremRain2"  # link proxy (typed FeaturePython)
  Detach = false
  LinkTransform = true
  LinkedObject = -> ShapeCopy [Face25]
  TreeRank = 0
  _LinkVersion = 1
  _Parent = -> Elements
FEATURE [Part::FeaturePython] Element009  label="FixM1"  # link proxy (typed FeaturePython)
  Detach = false
  LinkTransform = true
  LinkedObject = -> ShapeCopy [Edge168]
  TreeRank = 0
  _LinkVersion = 1
  _Parent = -> Elements
FEATURE [Part::FeaturePython] Element010  label="FixM2"  # link proxy (typed FeaturePython)
  Detach = false
  LinkTransform = true
  LinkedObject = -> ShapeCopy [Edge287]
  TreeRank = 0
  _LinkVersion = 1
  _Parent = -> Elements
